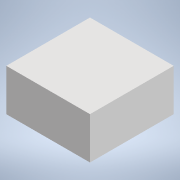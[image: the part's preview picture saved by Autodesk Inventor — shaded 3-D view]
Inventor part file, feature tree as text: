
AUTODESK INVENTOR PART (.ipt)
format: ipt  version: 2022 (Build 260153000, 153)  size: 86,528 bytes
history: native  units: in
note: dims shown in document units (in); Inventor stores cm internally (conversion verified against a paired STEP export)
features: extrude x1, sketch x1
ambient origin geometry x8: Origin, YZ Plane, XZ Plane, XY Plane, X Axis, Y Axis, Z Axis, Center Point
bodies: Solid1 (feature_tree)
feature tree (2):
  extrude  "Extrusion1"  Depth=3.0in
  sketch  "Sketch1"  dims[d0=3.0in d1=3.0in d2=1.5in d3=0.0in]
